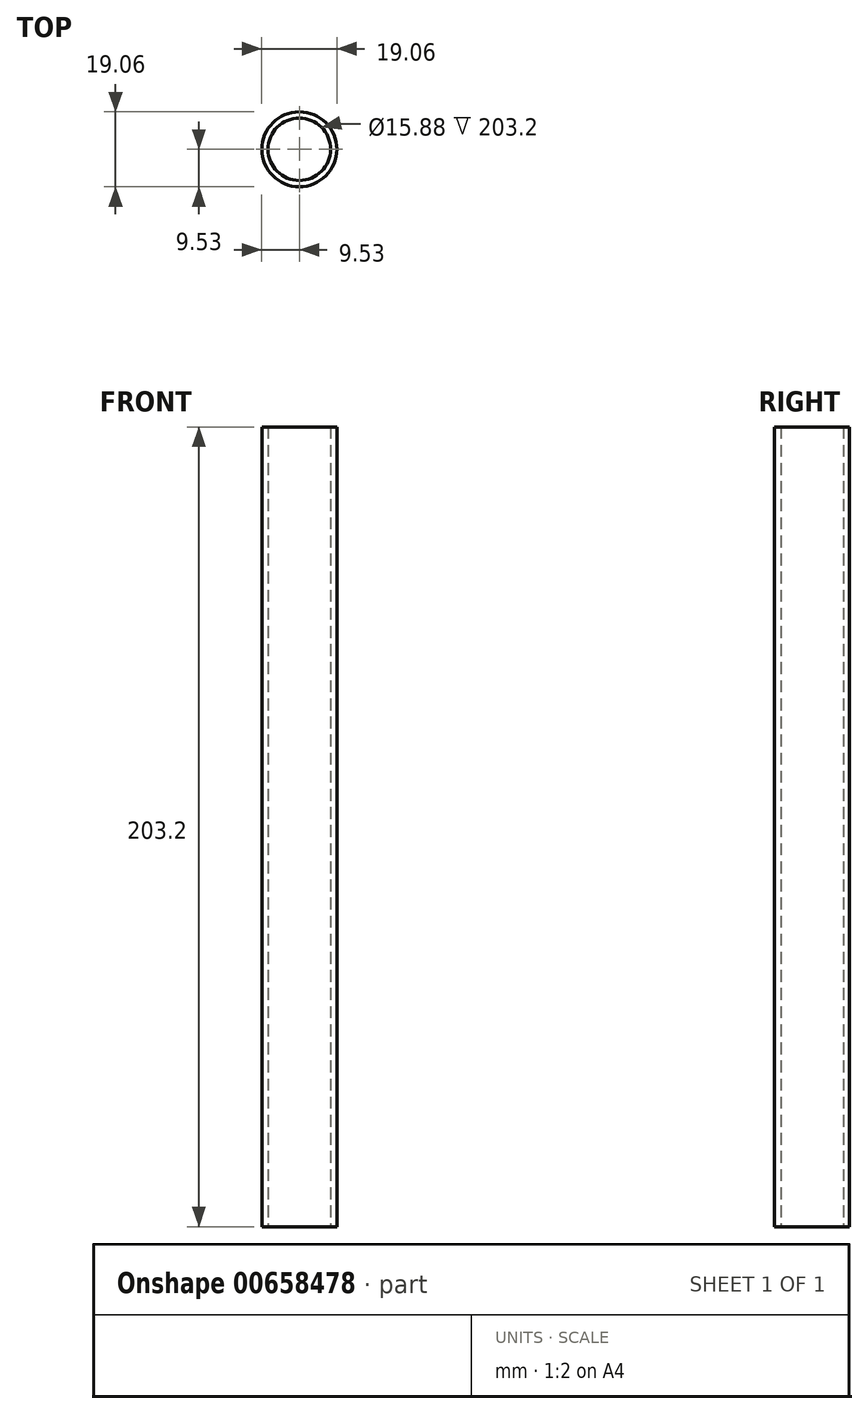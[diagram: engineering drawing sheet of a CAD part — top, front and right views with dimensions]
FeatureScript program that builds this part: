
annotation { "Feature Type Name" : "Feature", "Feature Type Description" : "" }
export const myFeature = defineFeature(function(context is Context, id is Id, definition is map)
    precondition{}
    {
        {
            var Q0;
            Q0=qCreatedBy(makeId("Top.planeOp"),FACE);
            var sketch = newSketch(context, id + "F0", { "sketchPlane" : qUnion([Q0])});
            skCircle(sketch, "E0", {"center": v(0, 0) * mm, "radius": 9.53 * mm});
            skCircle(sketch, "E1", {"center": v(0, 0) * mm, "radius": 7.94 * mm});
            skSolve(sketch);
        }
        {
            var Q0;
            Q0=makeQuery(id+"F0.imprint","IMPRINT",FACE,{"disambiguationData":[TD([[makeQuery(id+"F0.imprint","IMPRINT",EDGE,{"derivedFrom":sQuery(id+"F0.wireOp",EDGE,"E0")}),1.0]])]});
            extrude(context, id + "F1", {"entities" : qUnion([Q0]), "depth" : 152.4 * mm, "offsetDistance" : 25.4 * mm});
        }
        {
            var Q0;
            Q0=makeQuery(id+"F1.opExtrude","CAP_FACE",FACE,{"disambiguationData":[OSD([sQuery(id+"F0.wireOp",EDGE,"E0"),sQuery(id+"F0.wireOp",EDGE,"E1")])],"isStart":false});
            extrude(context, id + "F2", {"entities" : qUnion([Q0]), "operationType" : NewBodyOperationType.ADD, "depth" : 25.4 * mm, "offsetDistance" : 25.4 * mm});
        }
        {
            var Q0;
            Q0=makeQuery(id+"F1.opExtrude","CAP_FACE",FACE,{"disambiguationData":[OSD([sQuery(id+"F0.wireOp",EDGE,"E0"),sQuery(id+"F0.wireOp",EDGE,"E1")])],"isStart":true});
            extrude(context, id + "F3", {"entities" : qUnion([Q0]), "operationType" : NewBodyOperationType.ADD, "depth" : 25.4 * mm, "offsetDistance" : 25.4 * mm});
        }
    });
